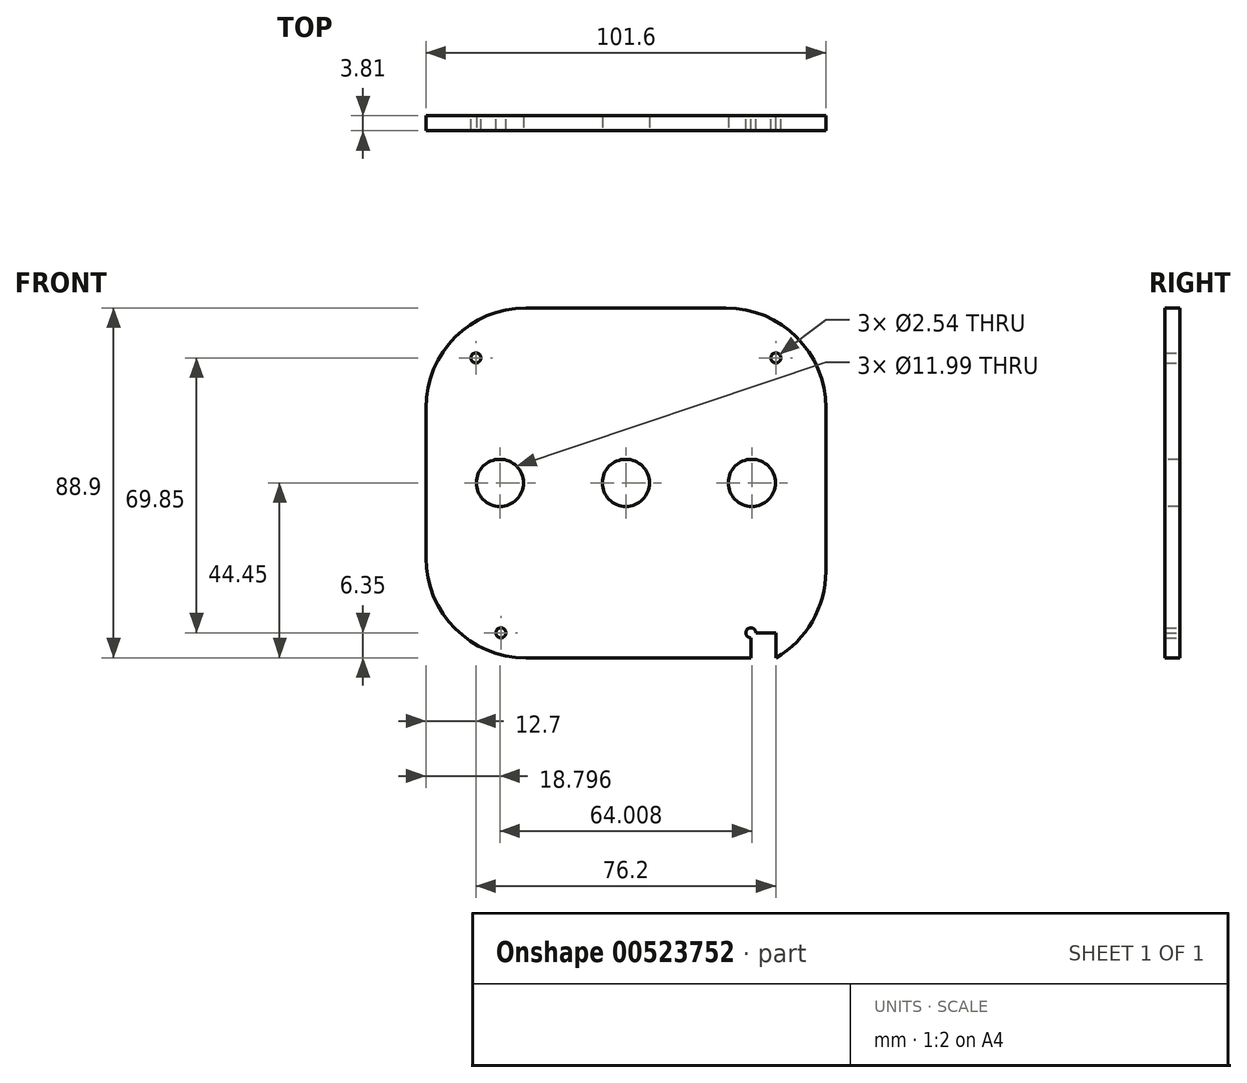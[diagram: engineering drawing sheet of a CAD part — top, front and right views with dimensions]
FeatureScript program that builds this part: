
annotation { "Feature Type Name" : "Feature", "Feature Type Description" : "" }
export const myFeature = defineFeature(function(context is Context, id is Id, definition is map)
    precondition{}
    {
        {
            var Q0;
            Q0=qCreatedBy(makeId("Front.planeOp"),FACE);
            var sketch = newSketch(context, id + "F0", { "sketchPlane" : qUnion([Q0])});
            skLineSegment(sketch, "E0.bottom", {"start": v(0, 0) * mm, "end": v(-76.2, 0) * mm});
            skLineSegment(sketch, "E0.top", {"start": v(0, -76.2) * mm, "end": v(-76.2, -76.2) * mm});
            skLineSegment(sketch, "E0.left", {"start": v(0, 0) * mm, "end": v(0, -76.2) * mm});
            skLineSegment(sketch, "E0.right", {"start": v(-76.2, 0) * mm, "end": v(-76.2, -76.2) * mm});
            skLineSegment(sketch, "E1", {"start": v(-76.2, -76.2) * mm, "end": v(-69.85, -76.2) * mm});
            skLineSegment(sketch, "E2", {"start": v(-69.85, -76.2) * mm, "end": v(-69.85, -69.85) * mm});
            skLineSegment(sketch, "E3", {"start": v(0, -76.2) * mm, "end": v(-6.35, -76.2) * mm});
            skLineSegment(sketch, "E4", {"start": v(-6.35, -76.2) * mm, "end": v(-6.35, -69.85) * mm});
            skLineSegment(sketch, "E5", {"start": v(-6.35, -69.85) * mm, "end": v(0, -69.85) * mm});
            skCircle(sketch, "E6", {"center": v(-6.35, -69.85) * mm, "radius": 1.27 * mm});
            skCircle(sketch, "E7", {"center": v(0, 0) * mm, "radius": 1.27 * mm});
            skCircle(sketch, "E8", {"center": v(-76.2, 0) * mm, "radius": 1.27 * mm});
            skCircle(sketch, "E9", {"center": v(-69.85, -69.85) * mm, "radius": 1.27 * mm});
            skLineSegment(sketch, "E10", {"start": v(-76.2, 0) * mm, "end": v(-88.9, 0) * mm});
            skLineSegment(sketch, "E11", {"start": v(-88.9, 0) * mm, "end": v(-88.9, 12.7) * mm});
            skLineSegment(sketch, "E12", {"start": v(0, 0) * mm, "end": v(12.7, 0) * mm});
            skLineSegment(sketch, "E13", {"start": v(12.7, 0) * mm, "end": v(12.7, 12.7) * mm});
            skLineSegment(sketch, "E14", {"start": v(0, -76.2) * mm, "end": v(12.7, -76.2) * mm});
            skLineSegment(sketch, "E15", {"start": v(-76.2, -76.2) * mm, "end": v(-88.9, -76.2) * mm});
            skLineSegment(sketch, "E16", {"start": v(-88.9, -76.2) * mm, "end": v(-88.9, 0) * mm});
            skLineSegment(sketch, "E17", {"start": v(-88.9, 12.7) * mm, "end": v(12.7, 12.7) * mm});
            skLineSegment(sketch, "E18", {"start": v(12.7, 0) * mm, "end": v(12.7, -76.2) * mm});
            skSolve(sketch);
        }
        {
            var Q0;
            {var subQ0=sQuery(id+"F0.wireOp",EDGE,"E11");Q0=makeQuery(id+"F0.imprint","IMPRINT",FACE,{"disambiguationData":[TD([[makeQuery(id+"F0.imprint","IMPRINT",EDGE,{"derivedFrom":subQ0}),-1.0]])]});}
            var Q1;
            {var subQ4=sQuery(id+"F0.wireOp",EDGE,"E15");Q1=makeQuery(id+"F0.imprint","IMPRINT",FACE,{"disambiguationData":[TD([[makeQuery(id+"F0.imprint","IMPRINT",EDGE,{"derivedFrom":subQ4}),-1.0]])]});}
            var Q2;
            {var subQ14=sQuery(id+"F0.wireOp",EDGE,"E0.top");Q2=makeQuery(id+"F0.imprint","IMPRINT",FACE,{"disambiguationData":[TD([[makeQuery(id+"F0.imprint","IMPRINT",EDGE,{"derivedFrom":subQ14}),-1.0]])]});}
            var Q3;
            {var subQ5=sQuery(id+"F0.wireOp",EDGE,"E3");Q3=makeQuery(id+"F0.imprint","IMPRINT",FACE,{"disambiguationData":[TD([[makeQuery(id+"F0.imprint","IMPRINT",EDGE,{"derivedFrom":subQ5}),-1.0]])]});}
            var Q4;
            {var subQ4=sQuery(id+"F0.wireOp",EDGE,"E14");Q4=makeQuery(id+"F0.imprint","IMPRINT",FACE,{"disambiguationData":[TD([[makeQuery(id+"F0.imprint","IMPRINT",EDGE,{"derivedFrom":subQ4}),1.0]])]});}
            extrude(context, id + "F1", {"entities" : qUnion([Q0, Q1, Q2, Q3, Q4]), "depth" : 3.8 * mm, "offsetDistance" : 25.4 * mm});
        }
        {
            var Q0;
            Q0=makeQuery(id+"F1.opExtrude","CAP_FACE",FACE,{"disambiguationData":[OSD([sQuery(id+"F0.wireOp",EDGE,"E0.top"),sQuery(id+"F0.wireOp",EDGE,"E1"),sQuery(id+"F0.wireOp",EDGE,"E3"),sQuery(id+"F0.wireOp",EDGE,"E6"),sQuery(id+"F0.wireOp",EDGE,"E7"),sQuery(id+"F0.wireOp",EDGE,"E8"),sQuery(id+"F0.wireOp",EDGE,"E9"),sQuery(id+"F0.wireOp",EDGE,"E11"),sQuery(id+"F0.wireOp",EDGE,"E13"),sQuery(id+"F0.wireOp",EDGE,"E14"),sQuery(id+"F0.wireOp",EDGE,"E15"),sQuery(id+"F0.wireOp",EDGE,"E16"),sQuery(id+"F0.wireOp",EDGE,"E17"),sQuery(id+"F0.wireOp",EDGE,"E18")])],"isStart":false});
            var sketch = newSketch(context, id + "F2", { "sketchPlane" : qUnion([Q0])});
            skLineSegment(sketch, "E19", {"start": v(-38.1, 12.7) * mm, "end": v(-38.1, -31.75) * mm});
            skLineSegment(sketch, "E20", {"start": v(-38.1, -31.75) * mm, "end": v(-6.1, -31.75) * mm});
            skLineSegment(sketch, "E21", {"start": v(-38.1, -31.75) * mm, "end": v(-70.1, -31.75) * mm});
            skCircle(sketch, "E22", {"center": v(-70.1, -31.75) * mm, "radius": 6 * mm});
            skCircle(sketch, "E23", {"center": v(-38.1, -31.75) * mm, "radius": 6 * mm});
            skCircle(sketch, "E24", {"center": v(-6.1, -31.75) * mm, "radius": 6 * mm});
            skSolve(sketch);
        }
        {
            var Q0;
            Q0=makeQuery(id+"F2.imprint","IMPRINT",FACE,{"disambiguationData":[TD([[makeQuery(id+"F2.imprint","IMPRINT",EDGE,{"derivedFrom":sQuery(id+"F2.wireOp",EDGE,"E22")}),1.0]])]});
            var Q1;
            {var subQ1=sQuery(id+"F2.wireOp",EDGE,"E19");var subQ3=sQuery(id+"F2.wireOp",EDGE,"E23");var subQ4=makeQuery(id+"F2.imprint","INTERSECT",VERTEX,{"derivedFrom":[subQ1,subQ3]});Q1=makeQuery(id+"F2.imprint","IMPRINT",FACE,{"disambiguationData":[TD([[makeQuery(id+"F2.imprint","IMPRINT",EDGE,{"disambiguationData":[TD([[subQ4,-1.0]])],"derivedFrom":subQ3}),1.0]])]});}
            var Q2;
            {var subQ1=sQuery(id+"F2.wireOp",EDGE,"E19");var subQ3=sQuery(id+"F2.wireOp",EDGE,"E23");var subQ4=makeQuery(id+"F2.imprint","INTERSECT",VERTEX,{"derivedFrom":[subQ1,subQ3]});Q2=makeQuery(id+"F2.imprint","IMPRINT",FACE,{"disambiguationData":[TD([[makeQuery(id+"F2.imprint","IMPRINT",EDGE,{"disambiguationData":[TD([[subQ4,1.0]])],"derivedFrom":subQ3}),1.0]])]});}
            var Q3;
            {var subQ1=sQuery(id+"F2.wireOp",EDGE,"E20");var subQ3=sQuery(id+"F2.wireOp",EDGE,"E23");var subQ4=makeQuery(id+"F2.imprint","INTERSECT",VERTEX,{"derivedFrom":[subQ1,subQ3]});Q3=makeQuery(id+"F2.imprint","IMPRINT",FACE,{"disambiguationData":[TD([[makeQuery(id+"F2.imprint","IMPRINT",EDGE,{"disambiguationData":[TD([[subQ4,1.0]])],"derivedFrom":subQ3}),1.0]])]});}
            var Q4;
            Q4=makeQuery(id+"F2.imprint","IMPRINT",FACE,{"disambiguationData":[TD([[makeQuery(id+"F2.imprint","IMPRINT",EDGE,{"derivedFrom":sQuery(id+"F2.wireOp",EDGE,"E24")}),1.0]])]});
            extrude(context, id + "F3", {"entities" : qUnion([Q0, Q1, Q2, Q3, Q4]), "operationType" : NewBodyOperationType.REMOVE, "oppositeDirection" : true, "depth" : 25.4 * mm, "offsetDistance" : 25.4 * mm});
        }
        {
            var Q0;
            Q0=makeQuery(id+"F1.opExtrude","SWEPT_EDGE",EDGE,{"disambiguationData":[OSD([sQuery(id+"F0.wireOp",EDGE,"E13"),sQuery(id+"F0.wireOp",EDGE,"E17")])]});
            var Q1;
            Q1=makeQuery(id+"F1.opExtrude","SWEPT_EDGE",EDGE,{"disambiguationData":[OSD([sQuery(id+"F0.wireOp",EDGE,"E11"),sQuery(id+"F0.wireOp",EDGE,"E17")])]});
            var Q2;
            Q2=makeQuery(id+"F1.opExtrude","SWEPT_EDGE",EDGE,{"disambiguationData":[OSD([sQuery(id+"F0.wireOp",EDGE,"E14"),sQuery(id+"F0.wireOp",EDGE,"E18")])]});
            var Q3;
            Q3=makeQuery(id+"F1.opExtrude","SWEPT_EDGE",EDGE,{"disambiguationData":[OSD([sQuery(id+"F0.wireOp",EDGE,"E15"),sQuery(id+"F0.wireOp",EDGE,"E16")])]});
            fillet(context, id + "F4", {"entities" : qUnion([Q0, Q1, Q2, Q3]), "radius" : 25.4 * mm, "tangentPropagation" : true, "allowEdgeOverflow" : false});
        }
    });
